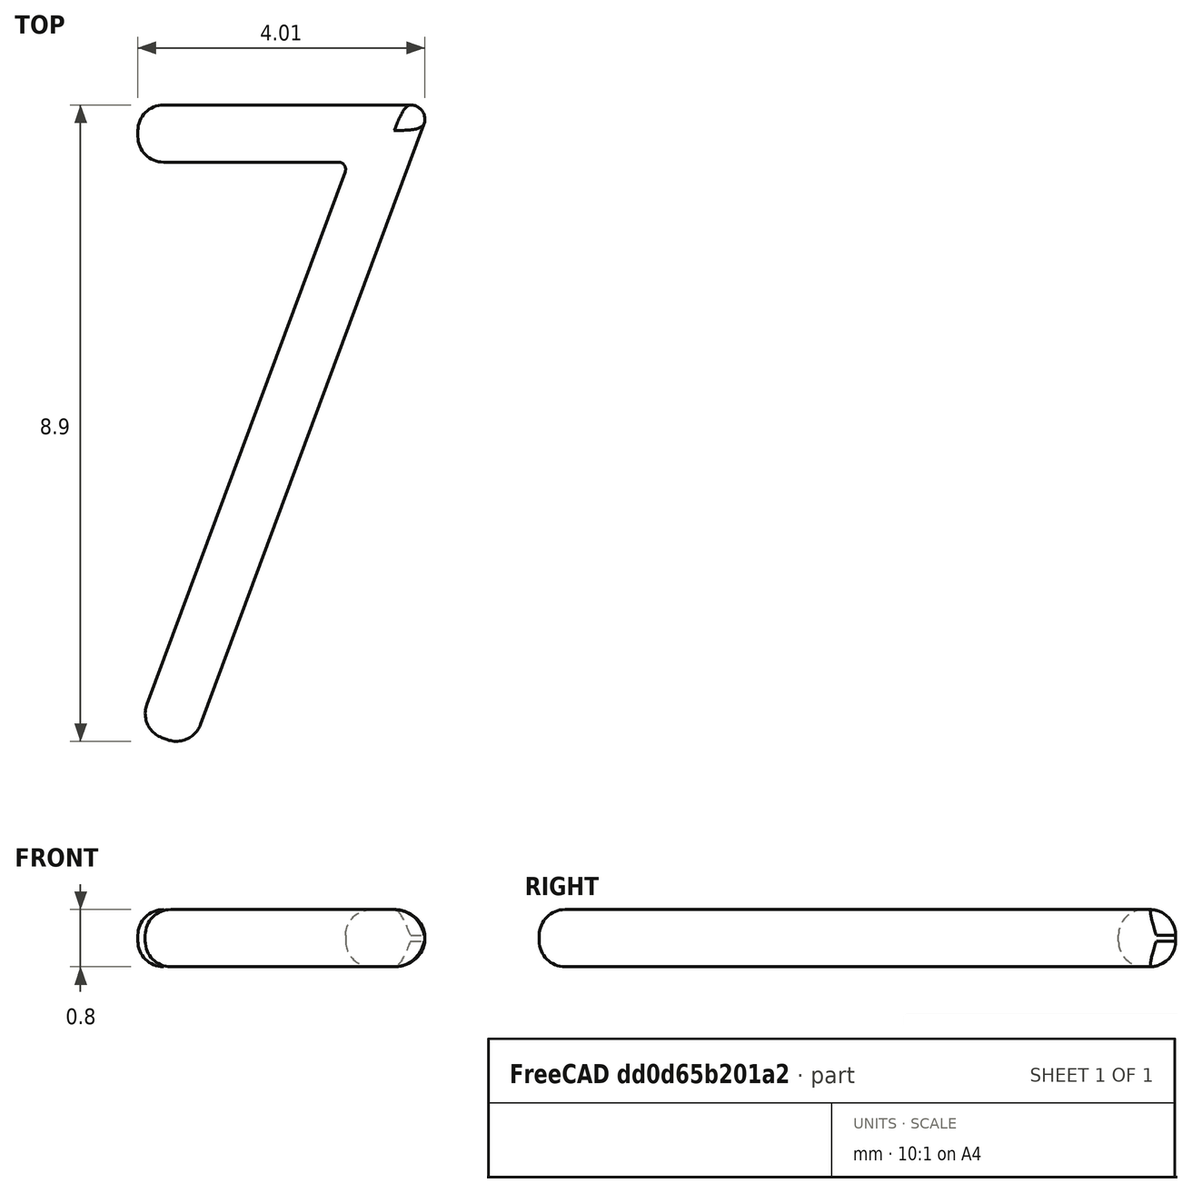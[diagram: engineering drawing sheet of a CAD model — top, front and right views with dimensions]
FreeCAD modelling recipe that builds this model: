
FCSTD DOCUMENT  (FreeCAD 0.16R6712 (Git))
Label: 7
License: All rights reserved
LicenseURL: http://en.wikipedia.org/wiki/All_rights_reserved
objects: Sketcher::SketchObject×1, PartDesign::Pad×1, PartDesign::Fillet×1, Mesh::Feature×1
note: 4 computed .brp shape members not serialized (recipe doc carries the construction recipe); baked Part::Feature solids carry a one-line shape summary decoded from their .brp

FEATURE [Sketcher::SketchObject] Sketch
  sketch-geometry (8):
    g0: LineSegment StartX=-2 StartY=9 StartZ=0 EndX=1.81257 EndY=9 EndZ=0
    g1: LineSegment StartX=2 StartY=8.73022 StartZ=0 EndX=-1.25027 EndY=0 EndZ=0
    g2: LineSegment StartX=-2 StartY=9 StartZ=0 EndX=-2 EndY=8.2 EndZ=0
    g3: LineSegment StartX=-2 StartY=8.2 StartZ=0 EndX=0.805018 EndY=8.2 EndZ=0
    g4: LineSegment StartX=0.898734 StartY=8.06511 StartZ=0 EndX=-2 EndY=0.279124 EndZ=0
    g5: LineSegment StartX=-2 StartY=0.279124 StartZ=0 EndX=-1.25027 EndY=0 EndZ=0
    g6: ArcOfCircle CenterX=0.805018 CenterY=8.1 CenterZ=0 NormalX=0 NormalY=0 NormalZ=1 Radius=0.1 StartAngle=5.92678 EndAngle=7.85398
    g7: ArcOfCircle CenterX=1.81257 CenterY=8.8 CenterZ=0 NormalX=0 NormalY=0 NormalZ=1 Radius=0.2 StartAngle=5.92678 EndAngle=7.85398
  constraints (22):
    c: Horizontal(g0)
    c: PointOnObject(g1,g-1)
    c: Coincident(g2,g0)
    c: Coincident(g3,g2)
    c: Horizontal(g3)
    c: Coincident(g5,g1)
    c: Coincident(g4,g5)
    c: Distance(g2,g0) = 0.8
    c: Distance(g1,g4) = 0.8
    c: Perpendicular(g5,g4)
    c: Perpendicular(g3,g2)
    c: DistanceX(g-2,g0) = -2
    c: DistanceX(g-2,g4) = -2
    c: Perpendicular(g5,g1)
    c: Tangent(g3,g6) = 1.5708
    c: Tangent(g4,g6) = 1.5708
    c: Tangent(g0,g7) = 1.5708
    c: Tangent(g1,g7) = 1.5708
    c: Radius(g6) = 0.1
    c: Radius(g7) = 0.2
    c: DistanceY(g-1,g0) = 9
    c: DistanceX(g-2,g1) = 2
FEATURE [PartDesign::Pad] Pad
  Length = 0.8
  Length2 = 100
  Midplane = true
  Sketch = -> Sketch
  Type = 0
FEATURE [PartDesign::Fillet] Fillet
  Base = -> Pad [Edge4,Edge7,Edge10,Edge13,Edge16,Edge19,Edge22,Edge24,Edge3,Edge6,Edge9,Edge12,Edge15,Edge18,Edge21,Edge23,Edge1,Edge2,Edge14,Edge11]
  Radius = 0.36
FEATURE [Mesh::Feature] Mesh  label="Fillet (Meshed)"
